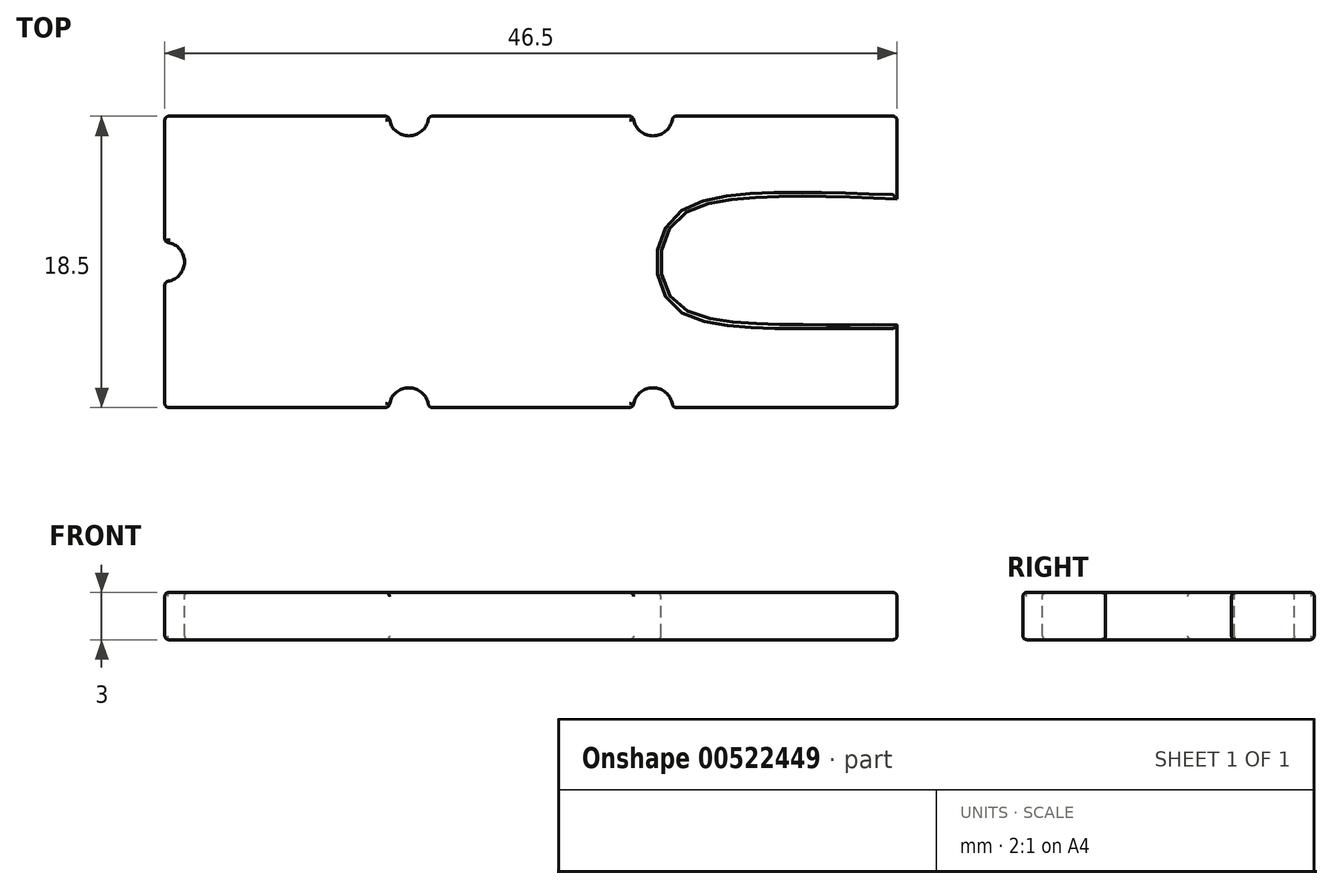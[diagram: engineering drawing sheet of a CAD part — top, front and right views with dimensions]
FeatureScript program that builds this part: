
annotation { "Feature Type Name" : "Feature", "Feature Type Description" : "" }
export const myFeature = defineFeature(function(context is Context, id is Id, definition is map)
    precondition{}
    {
        {
            var Q0;
            Q0=qCreatedBy(makeId("Top.planeOp"),FACE);
            var sketch = newSketch(context, id + "F0", { "sketchPlane" : qUnion([Q0])});
            skLineSegment(sketch, "E0.bottom", {"start": v(0, 0) * mm, "end": v(46.5, 0) * mm});
            skLineSegment(sketch, "E0.top", {"start": v(0, -18.5) * mm, "end": v(46.5, -18.5) * mm});
            skLineSegment(sketch, "E0.left", {"start": v(0, 0) * mm, "end": v(0, -18.5) * mm});
            skLineSegment(sketch, "E0.right", {"start": v(46.5, 0) * mm, "end": v(46.5, -18.5) * mm});
            skLineSegment(sketch, "E1.left", {"start": v(0, -18.5) * mm, "end": v(0, -18.5) * mm});
            skLineSegment(sketch, "E1.right", {"start": v(46.5, -18.5) * mm, "end": v(46.5, -18.5) * mm});
            skFitSpline(sketch, "E2", {"points": [v(46.5, -5.25) * mm, v(34.58, -5.55) * mm, v(32.15, -6.98) * mm, v(31.5, -9.25) * mm, v(32.15, -11.53) * mm, v(34.58, -12.85) * mm, v(46.5, -13.25) * mm], "startDerivative": vector(-60.2, 2.57) * mm, "endDerivative": vector(60.19, -0.34) * mm});
            skPoint(sketch, "E3", {"position": v(46.5, -9.25) * mm});
            skSolve(sketch);
        }
        {
            var Q0;
            Q0=makeQuery(id+"F0.imprint","IMPRINT",FACE,{"disambiguationData":[TD([[makeQuery(id+"F0.imprint","IMPRINT",EDGE,{"derivedFrom":sQuery(id+"F0.wireOp",EDGE,"E0.bottom")}),-1.0]])]});
            extrude(context, id + "F1", {"entities" : qUnion([Q0]), "depth" : 3 * mm, "offsetDistance" : 25 * mm});
        }
        {
            var Q0;
            Q0=qCreatedBy(makeId("Top.planeOp"),FACE);
            cPlane(context, id + "F2", {"entities" : qUnion([Q0]), "cplaneType" : CPlaneType.OFFSET, "offset" : 10 * mm, "width" : 150 * mm, "height" : 150 * mm});
        }
        {
            var Q0;
            Q0=qCreatedBy(id+"F2.planeOp",FACE);
            var sketch = newSketch(context, id + "F3", { "sketchPlane" : qUnion([Q0])});
            skCircle(sketch, "E4", {"center": v(0, -9.25) * mm, "radius": 1.25 * mm});
            skSolve(sketch);
        }
        {
            var Q0;
            Q0=qCreatedBy(id+"F2.planeOp",FACE);
            var sketch = newSketch(context, id + "F4", { "sketchPlane" : qUnion([Q0])});
            skCircle(sketch, "E5", {"center": v(15.5, 0) * mm, "radius": 1.25 * mm});
            skCircle(sketch, "E6", {"center": v(31, 0) * mm, "radius": 1.25 * mm});
            skCircle(sketch, "E7", {"center": v(15.5, -18.5) * mm, "radius": 1.25 * mm});
            skCircle(sketch, "E8", {"center": v(31, -18.5) * mm, "radius": 1.25 * mm});
            skFitSpline(sketch, "E9", {"points": [v(46.5, 1.37) * mm, v(36.2, -5.16) * mm, v(34.02, -5.5) * mm, v(32.66, -6.27) * mm, v(31.5, -2.63) * mm, v(32.82, -12.26) * mm, v(36.02, -13.03) * mm, v(46.48, -6.63) * mm], "startDerivative": vector(-50.23, 0.71) * mm, "endDerivative": vector(51.53, 0.46) * mm});
            skSolve(sketch);
        }
        {
            var Q0;
            Q0 = qSketchRegion(id + "F3", true);
            var Q1;
            Q1 = qSketchRegion(id + "F4", true);
            extrude(context, id + "F5", {"entities" : qUnion([Q0, Q1]), "operationType" : NewBodyOperationType.REMOVE, "oppositeDirection" : true, "depth" : 25 * mm, "offsetDistance" : 25 * mm});
        }
        {
            var Q0;
            Q0=makeQuery(id+"F1.opExtrude","CAP_FACE",FACE,{"disambiguationData":[OSD([sQuery(id+"F0.wireOp",EDGE,"E0.bottom"),sQuery(id+"F0.wireOp",EDGE,"E0.left"),sQuery(id+"F0.wireOp",EDGE,"E0.right"),sQuery(id+"F0.wireOp",EDGE,"E0.top")])],"isStart":false});
            var Q1;
            Q1=makeQuery(id+"F1.opExtrude","CAP_FACE",FACE,{"disambiguationData":[OSD([sQuery(id+"F0.wireOp",EDGE,"E0.bottom"),sQuery(id+"F0.wireOp",EDGE,"E0.left"),sQuery(id+"F0.wireOp",EDGE,"E0.right"),sQuery(id+"F0.wireOp",EDGE,"E0.top")])],"isStart":true});
            var Q2;
            Q2=makeQuery(id+"F1.opExtrude","SWEPT_EDGE",EDGE,{"disambiguationData":[OSD([sQuery(id+"F0.wireOp",EDGE,"E0.bottom"),sQuery(id+"F0.wireOp",EDGE,"E0.right")])]});
            var Q3;
            Q3=makeQuery(id+"F5.boolean.opBoolean","INTERSECT",EDGE,{"disambiguationData":[OD(0.0)],"derivedFrom":[makeQuery(id+"F1.opExtrude","SWEPT_FACE",FACE,{"disambiguationData":[OSD([sQuery(id+"F0.wireOp",EDGE,"E0.right")])]}),makeQuery(id+"F5.opExtrude","SWEPT_FACE",FACE,{"disambiguationData":[OSD([sQuery(id+"F4.wireOp",EDGE,"BWA5S98U-SA1p-oO7t-RmQM-WKwiQEXaPlnO")])]})]});
            var Q4;
            Q4=makeQuery(id+"F5.boolean.opBoolean","INTERSECT",EDGE,{"disambiguationData":[OD(1.0)],"derivedFrom":[makeQuery(id+"F1.opExtrude","SWEPT_FACE",FACE,{"disambiguationData":[OSD([sQuery(id+"F0.wireOp",EDGE,"E0.right")])]}),makeQuery(id+"F5.opExtrude","SWEPT_FACE",FACE,{"disambiguationData":[OSD([sQuery(id+"F4.wireOp",EDGE,"BWA5S98U-SA1p-oO7t-RmQM-WKwiQEXaPlnO")])]})]});
            var Q5;
            Q5=makeQuery(id+"F1.opExtrude","SWEPT_EDGE",EDGE,{"disambiguationData":[OSD([sQuery(id+"F0.wireOp",EDGE,"E0.right"),sQuery(id+"F0.wireOp",EDGE,"E0.top")])]});
            var Q6;
            Q6=makeQuery(id+"F5.boolean.opBoolean","INTERSECT",EDGE,{"disambiguationData":[OD(0.0)],"derivedFrom":[makeQuery(id+"F1.opExtrude","SWEPT_FACE",FACE,{"disambiguationData":[OSD([sQuery(id+"F0.wireOp",EDGE,"E0.top")])]}),makeQuery(id+"F5.opExtrude","SWEPT_FACE",FACE,{"disambiguationData":[OSD([sQuery(id+"F4.wireOp",EDGE,"E8")])]})]});
            var Q7;
            Q7=makeQuery(id+"F5.boolean.opBoolean","INTERSECT",EDGE,{"disambiguationData":[OD(1.0)],"derivedFrom":[makeQuery(id+"F1.opExtrude","SWEPT_FACE",FACE,{"disambiguationData":[OSD([sQuery(id+"F0.wireOp",EDGE,"E0.top")])]}),makeQuery(id+"F5.opExtrude","SWEPT_FACE",FACE,{"disambiguationData":[OSD([sQuery(id+"F4.wireOp",EDGE,"E8")])]})]});
            var Q8;
            Q8=makeQuery(id+"F5.boolean.opBoolean","INTERSECT",EDGE,{"disambiguationData":[OD(0.0)],"derivedFrom":[makeQuery(id+"F1.opExtrude","SWEPT_FACE",FACE,{"disambiguationData":[OSD([sQuery(id+"F0.wireOp",EDGE,"E0.top")])]}),makeQuery(id+"F5.opExtrude","SWEPT_FACE",FACE,{"disambiguationData":[OSD([sQuery(id+"F4.wireOp",EDGE,"E7")])]})]});
            var Q9;
            Q9=makeQuery(id+"F5.boolean.opBoolean","INTERSECT",EDGE,{"disambiguationData":[OD(1.0)],"derivedFrom":[makeQuery(id+"F1.opExtrude","SWEPT_FACE",FACE,{"disambiguationData":[OSD([sQuery(id+"F0.wireOp",EDGE,"E0.top")])]}),makeQuery(id+"F5.opExtrude","SWEPT_FACE",FACE,{"disambiguationData":[OSD([sQuery(id+"F4.wireOp",EDGE,"E7")])]})]});
            var Q10;
            Q10=makeQuery(id+"F1.opExtrude","SWEPT_EDGE",EDGE,{"disambiguationData":[OSD([sQuery(id+"F0.wireOp",EDGE,"E0.left"),sQuery(id+"F0.wireOp",EDGE,"E0.top")])]});
            var Q11;
            Q11=makeQuery(id+"F5.boolean.opBoolean","INTERSECT",EDGE,{"disambiguationData":[OD(1.0)],"derivedFrom":[makeQuery(id+"F1.opExtrude","SWEPT_FACE",FACE,{"disambiguationData":[OSD([sQuery(id+"F0.wireOp",EDGE,"E0.left")])]}),makeQuery(id+"F5.opExtrude","SWEPT_FACE",FACE,{"disambiguationData":[OSD([sQuery(id+"F3.wireOp",EDGE,"E4")])]})]});
            var Q12;
            Q12=makeQuery(id+"F5.boolean.opBoolean","INTERSECT",EDGE,{"disambiguationData":[OD(0.0)],"derivedFrom":[makeQuery(id+"F1.opExtrude","SWEPT_FACE",FACE,{"disambiguationData":[OSD([sQuery(id+"F0.wireOp",EDGE,"E0.left")])]}),makeQuery(id+"F5.opExtrude","SWEPT_FACE",FACE,{"disambiguationData":[OSD([sQuery(id+"F3.wireOp",EDGE,"E4")])]})]});
            var Q13;
            Q13=makeQuery(id+"F1.opExtrude","SWEPT_EDGE",EDGE,{"disambiguationData":[OSD([sQuery(id+"F0.wireOp",EDGE,"E0.bottom"),sQuery(id+"F0.wireOp",EDGE,"E0.left")])]});
            var Q14;
            Q14=makeQuery(id+"F5.boolean.opBoolean","INTERSECT",EDGE,{"disambiguationData":[OD(0.0)],"derivedFrom":[makeQuery(id+"F1.opExtrude","SWEPT_FACE",FACE,{"disambiguationData":[OSD([sQuery(id+"F0.wireOp",EDGE,"E0.bottom")])]}),makeQuery(id+"F5.opExtrude","SWEPT_FACE",FACE,{"disambiguationData":[OSD([sQuery(id+"F4.wireOp",EDGE,"E5")])]})]});
            var Q15;
            Q15=makeQuery(id+"F5.boolean.opBoolean","INTERSECT",EDGE,{"disambiguationData":[OD(1.0)],"derivedFrom":[makeQuery(id+"F1.opExtrude","SWEPT_FACE",FACE,{"disambiguationData":[OSD([sQuery(id+"F0.wireOp",EDGE,"E0.bottom")])]}),makeQuery(id+"F5.opExtrude","SWEPT_FACE",FACE,{"disambiguationData":[OSD([sQuery(id+"F4.wireOp",EDGE,"E5")])]})]});
            var Q16;
            Q16=makeQuery(id+"F5.boolean.opBoolean","INTERSECT",EDGE,{"disambiguationData":[OD(1.0)],"derivedFrom":[makeQuery(id+"F1.opExtrude","SWEPT_FACE",FACE,{"disambiguationData":[OSD([sQuery(id+"F0.wireOp",EDGE,"E0.bottom")])]}),makeQuery(id+"F5.opExtrude","SWEPT_FACE",FACE,{"disambiguationData":[OSD([sQuery(id+"F4.wireOp",EDGE,"E6")])]})]});
            var Q17;
            Q17=makeQuery(id+"F5.boolean.opBoolean","INTERSECT",EDGE,{"disambiguationData":[OD(0.0)],"derivedFrom":[makeQuery(id+"F1.opExtrude","SWEPT_FACE",FACE,{"disambiguationData":[OSD([sQuery(id+"F0.wireOp",EDGE,"E0.bottom")])]}),makeQuery(id+"F5.opExtrude","SWEPT_FACE",FACE,{"disambiguationData":[OSD([sQuery(id+"F4.wireOp",EDGE,"E6")])]})]});
            fillet(context, id + "F6", {"entities" : qUnion([Q0, Q1, Q2, Q3, Q4, Q5, Q6, Q7, Q8, Q9, Q10, Q11, Q12, Q13, Q14, Q15, Q16, Q17]), "radius" : 0.25 * mm, "tangentPropagation" : true, "allowEdgeOverflow" : false});
        }
    });
